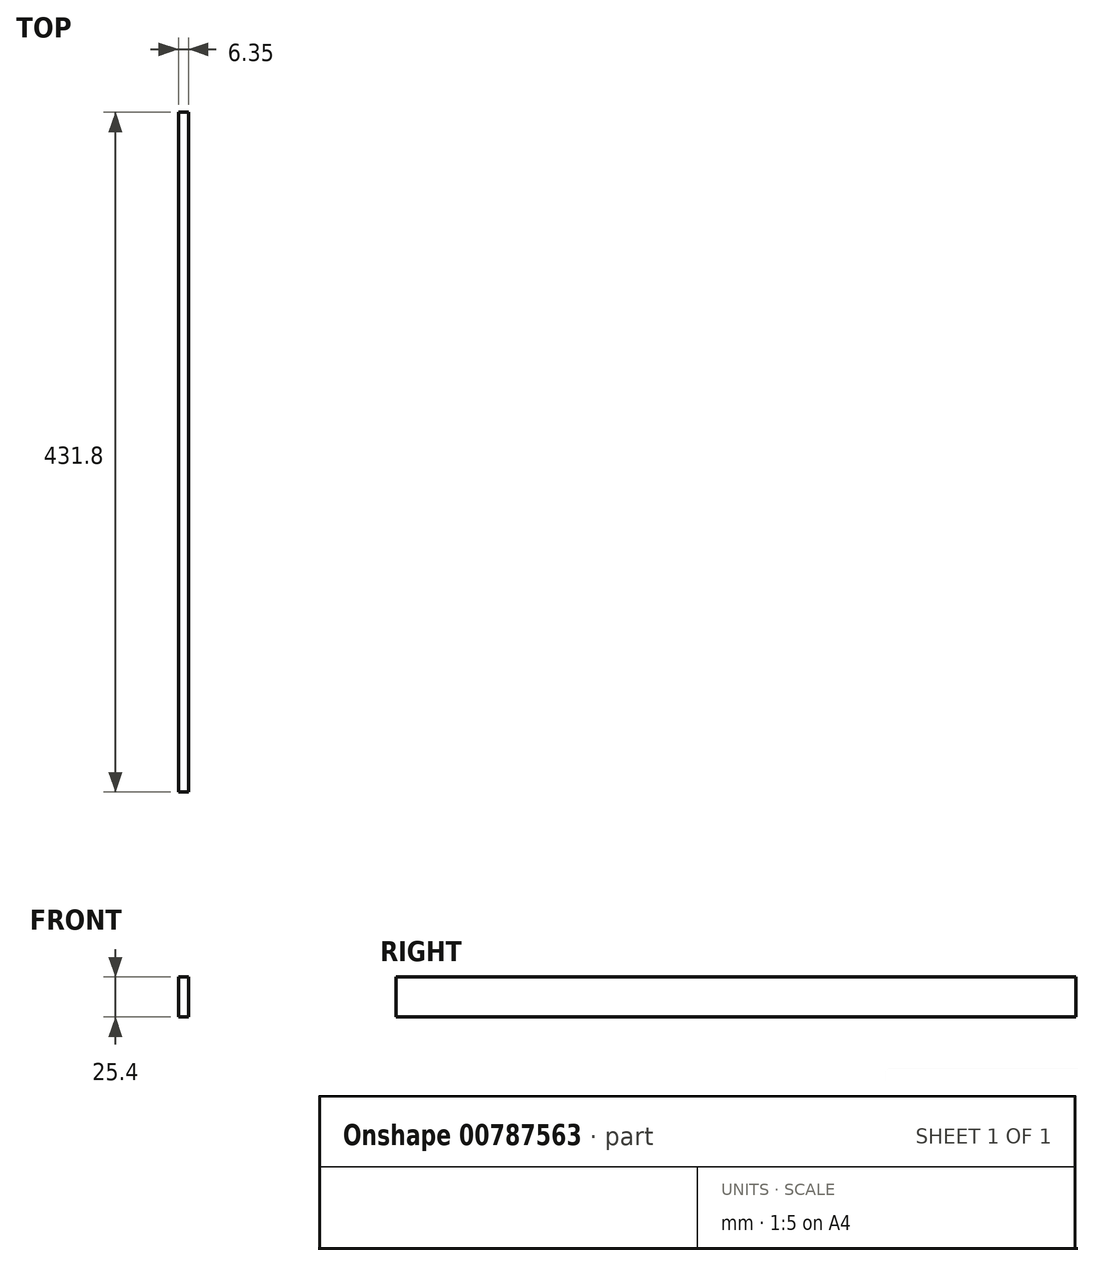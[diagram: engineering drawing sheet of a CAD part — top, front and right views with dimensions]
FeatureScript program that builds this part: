
annotation { "Feature Type Name" : "Feature", "Feature Type Description" : "" }
export const myFeature = defineFeature(function(context is Context, id is Id, definition is map)
    precondition{}
    {
        {
            var Q0;
            Q0=qCreatedBy(makeId("Right.planeOp"),FACE);
            var sketch = newSketch(context, id + "F0", { "sketchPlane" : qUnion([Q0])});
            skLineSegment(sketch, "E0.bottom", {"start": v(215.9, -12.7) * mm, "end": v(-215.9, -12.7) * mm});
            skLineSegment(sketch, "E0.top", {"start": v(215.9, 12.7) * mm, "end": v(-215.9, 12.7) * mm});
            skLineSegment(sketch, "E0.left", {"start": v(215.9, -12.7) * mm, "end": v(215.9, 12.7) * mm});
            skLineSegment(sketch, "E0.right", {"start": v(-215.9, -12.7) * mm, "end": v(-215.9, 12.7) * mm});
            skPoint(sketch, "E0.middle", {"position": v(0, 0) * mm});
            skSolve(sketch);
        }
        {
            var Q0;
            Q0 = qSketchRegion(id + "F0", true);
            extrude(context, id + "F1", {"entities" : qUnion([Q0]), "depth" : 6.35 * mm, "offsetDistance" : 25.4 * mm});
        }
    });
